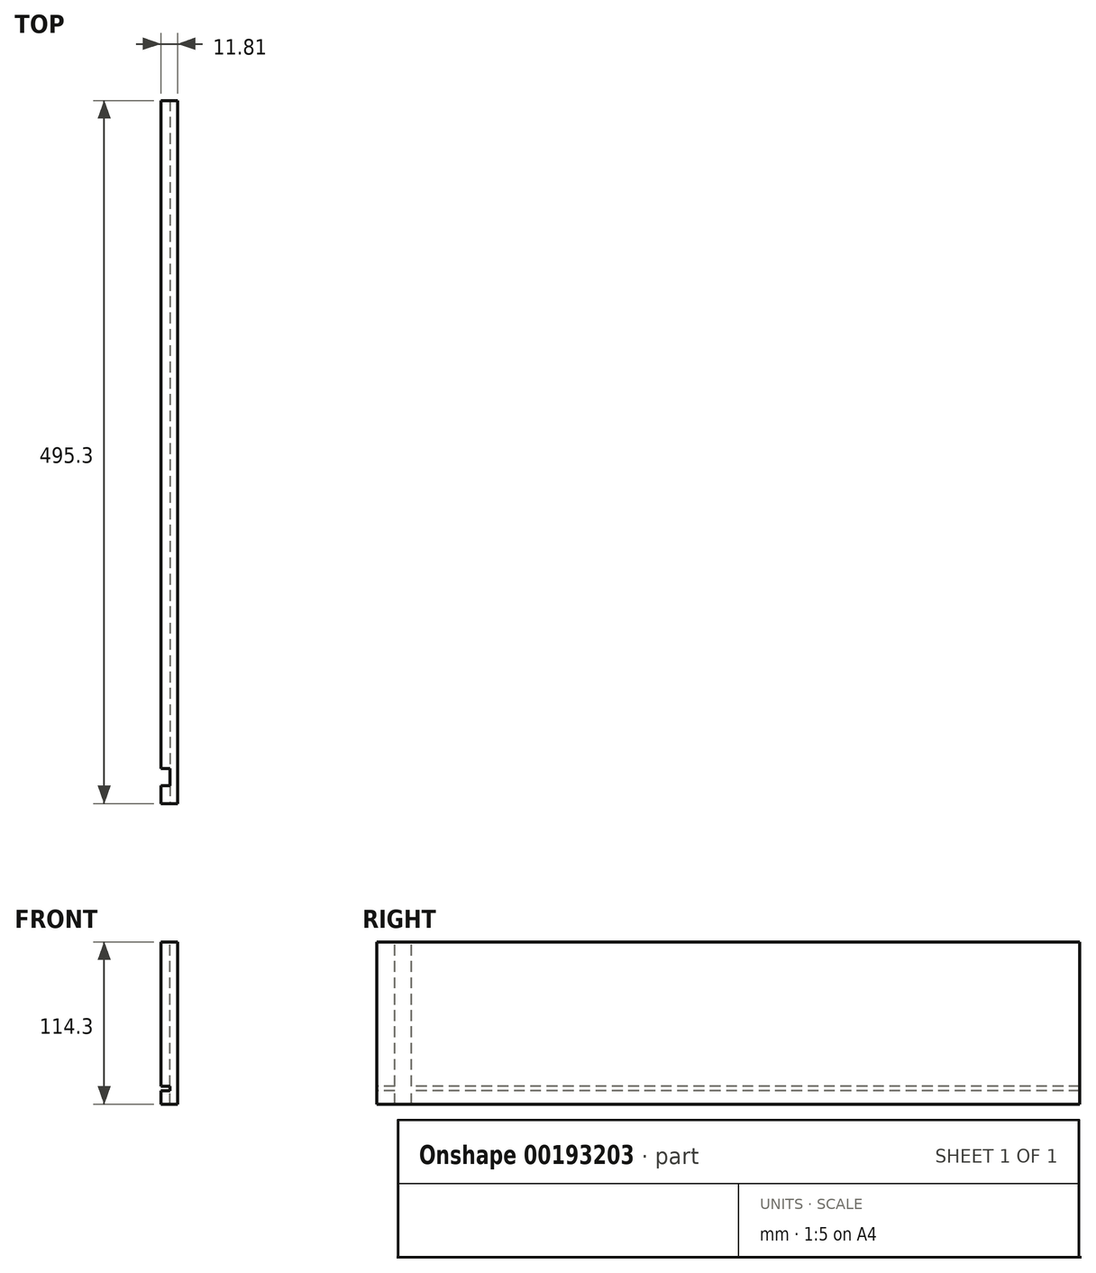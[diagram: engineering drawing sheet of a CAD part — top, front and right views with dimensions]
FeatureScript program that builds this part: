
annotation { "Feature Type Name" : "Feature", "Feature Type Description" : "" }
export const myFeature = defineFeature(function(context is Context, id is Id, definition is map)
    precondition{}
    {
        {
            var Q0;
            Q0=qCreatedBy(makeId("Front.planeOp"),FACE);
            var sketch = newSketch(context, id + "F0", { "sketchPlane" : qUnion([Q0])});
            skLineSegment(sketch, "E0.bottom", {"start": v(0, 0) * mm, "end": v(11.81, 0) * mm});
            skLineSegment(sketch, "E0.top", {"start": v(0, -114.3) * mm, "end": v(11.81, -114.3) * mm});
            skLineSegment(sketch, "E0.left", {"start": v(0, 0) * mm, "end": v(0, -101.6) * mm});
            skLineSegment(sketch, "E0.right", {"start": v(11.81, 0) * mm, "end": v(11.81, -114.3) * mm});
            skLineSegment(sketch, "E1.bottom", {"start": v(0, -101.6) * mm, "end": v(6.35, -101.6) * mm});
            skLineSegment(sketch, "E1.top", {"start": v(0, -104.78) * mm, "end": v(6.35, -104.78) * mm});
            skLineSegment(sketch, "E1.right", {"start": v(6.35, -101.6) * mm, "end": v(6.35, -104.78) * mm});
            skLineSegment(sketch, "E2.trimOffspring", {"start": v(0, -104.78) * mm, "end": v(0, -114.3) * mm});
            skSolve(sketch);
        }
        {
            var Q0;
            Q0=qSketchRegion(id+"F0",true);
            extrude(context, id + "F1", {"entities" : qUnion([Q0]), "oppositeDirection" : true, "depth" : 495.3 * mm});
        }
        {
            var Q0;
            Q0=makeQuery(id+"F1.opExtrude","SWEPT_FACE",FACE,{"disambiguationData":[OSD([sQuery(id+"F0.wireOp",EDGE,"E0.bottom")])]});
            var sketch = newSketch(context, id + "F2", { "sketchPlane" : qUnion([Q0])});
            skLineSegment(sketch, "E3.bottom", {"start": v(0, 12.7) * mm, "end": v(6.35, 12.7) * mm});
            skLineSegment(sketch, "E3.top", {"start": v(0, 24.51) * mm, "end": v(6.35, 24.51) * mm});
            skLineSegment(sketch, "E3.left", {"start": v(0, 12.7) * mm, "end": v(0, 24.51) * mm});
            skLineSegment(sketch, "E3.right", {"start": v(6.35, 12.7) * mm, "end": v(6.35, 24.51) * mm});
            skSolve(sketch);
        }
        {
            var Q0;
            Q0=qSketchRegion(id+"F2",true);
            extrude(context, id + "F3", {"entities" : qUnion([Q0]), "operationType" : NewBodyOperationType.REMOVE, "endBound" : BoundingType.THROUGH_ALL, "oppositeDirection" : true, "depth" : 25.4 * mm});
        }
    });
